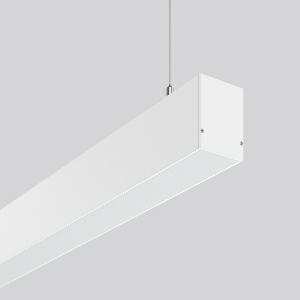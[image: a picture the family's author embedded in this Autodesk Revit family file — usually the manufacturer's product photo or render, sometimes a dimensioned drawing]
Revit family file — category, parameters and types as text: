
# Revit family: less_is_more_50_312315_002_e754
name_source: partatom
category: Lighting Fixtures
units: mm (PartAtom-declared; Revit-internal decimal feet)

## family parameters
Cut with Voids When Loaded = No
Host = Face
Light Source = No
Part Type = Normal
Room Calculation Point = No
Round Connector Dimension = Use Diameter
Shared = No

## types (1)
- LESS IS MORE 50 (1 x LED Modul 830, 5400 lm, 3000)
    Apparent Load = 47 VA
    CIE Flux Codes = 48 79 95 100 100
    Color Rendering = 80
    Color Temperature = 3000
    Default Elevation = 1800 mm
    Description = Series: LESS IS MORE 50
Linear pendant luminaire for aesthetically sophisticated lighting. Housing: extruded aluminium profile, powder-coated. End cap aluminium powder-coated. Canopy made of aluminium, powder-coated. Diffuser made of non-yellowing plastic (PMMA), opal. Direct light emission. Suitable for pendant. 2-point steel cable suspension freely positionable and infinitely height-adjustable. Special lengths available on request. LED unit with integrated converter interchangeable and removable. Suitable for through-wiring. With sensors or as a safety luminaire on request. 
Colour: traffic white, matt (RAL 9016)
Length: 1967 mm
Width: 57 mm
Height: 75 mm
Suspension length: 2000 mm
Lamp: LED
Socket: without socket
Colour temperature: 3000K
Colour rendering index (CRI): 80
System power: 47 W
Rated luminous flux: 5400 lm
Luminous efficiency: 115 lm/W
Control gear: Regulated power supply
Protection class: I
Type of protection: IP 20
    Height = 75 mm
    Lamp = 1 x LED Modul 830
    Lamp Light Flux = 5400 lm
    Lamp count = 1
    Length = 1967 mm
    Lifetime = 50000 h
    Luminous efficacy = 115 lm/W
    Manufacturer = RZB
    ModVariant = No
    Model = 312315.002
    Mounting Place = Ceiling
    Mounting Type = Pendant
    Number of Poles = 1
    OnlyDefault = Yes
    Power Factor = 1
    Product Name = LESS IS MORE 50
    Product group = Pendant LED linear luminaires
    ProductGroupID = 907
    Protection Class = Protection class I
    Protection Degree = IP 20
    RLX_Detail_Level = 1
    RLX_Emergency_Light_Flux = 0 lm
    RLX_Emergency_Type = 0
    RLX_Emergency_Type_DB = No
    RlxData = <blob elided: 20589 chars, md5=affbc031>
    Socket = socket
    Standby Power = 0 W
    System Light Flux = 5400 lm
    System Power = 47 W
    Type Comments = Product without accessories
    Type Image = 312318.002.jpg
    URL = http://relux.com
    VarID = ---
    Voltage = 230 V
    Voltage Range = 220-240 V
    Weight = 0.00 kg
    Width = 57 mm

## geometry (parser evidence)
native form markers: Blend x4, Sweep x12
no freeform markers — native parametric forms only
